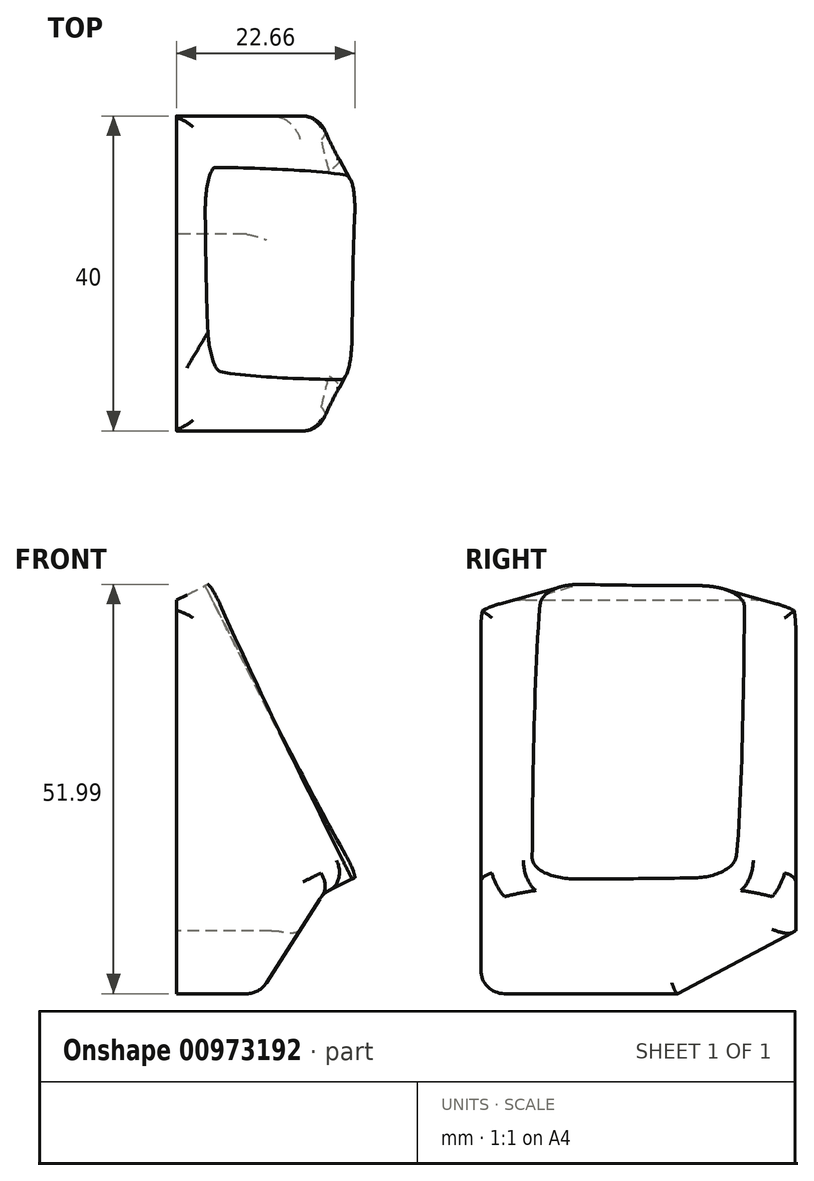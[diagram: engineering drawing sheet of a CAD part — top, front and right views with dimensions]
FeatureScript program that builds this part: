
annotation { "Feature Type Name" : "Feature", "Feature Type Description" : "" }
export const myFeature = defineFeature(function(context is Context, id is Id, definition is map)
    precondition{}
    {
        {
            var Q0;
            Q0=qCreatedBy(makeId("Front.planeOp"),FACE);
            var sketch = newSketch(context, id + "F0", { "sketchPlane" : qUnion([Q0])});
            skLineSegment(sketch, "E0", {"start": v(-46.03, 26.47) * mm, "end": v(-46.03, -23.53) * mm});
            skPoint(sketch, "E1", {"position": v(-35.49, -23.53) * mm});
            skPoint(sketch, "E2", {"position": v(-27.37, -10.8) * mm});
            skLineSegment(sketch, "E3", {"start": v(-27.37, -10.8) * mm, "end": v(-35.49, -23.53) * mm});
            skLineSegment(sketch, "E4", {"start": v(-46.03, -23.53) * mm, "end": v(-35.49, -23.53) * mm});
            skLineSegment(sketch, "E5", {"start": v(-46.03, 26.47) * mm, "end": v(-27.37, -10.8) * mm});
            skLineSegment(sketch, "E6", {"start": v(-46.03, 26.47) * mm, "end": v(-41.55, 28.7) * mm});
            skLineSegment(sketch, "E7", {"start": v(-27.37, -10.8) * mm, "end": v(-22.9, -8.55) * mm});
            skLineSegment(sketch, "E8", {"start": v(-41.55, 28.7) * mm, "end": v(-22.9, -8.55) * mm});
            skSolve(sketch);
        }
        {
            var Q0;
            Q0=makeQuery(id+"F0.imprint","IMPRINT",FACE,{"disambiguationData":[TD([[makeQuery(id+"F0.imprint","IMPRINT",EDGE,{"derivedFrom":sQuery(id+"F0.wireOp",EDGE,"E0")}),1.0]])]});
            extrude(context, id + "F1", {"entities" : qUnion([Q0]), "depth" : 40 * mm, "offsetDistance" : 25.4 * mm});
        }
        {
            var Q0;
            Q0=makeQuery(id+"F0.imprint","IMPRINT",FACE,{"disambiguationData":[TD([[makeQuery(id+"F0.imprint","IMPRINT",EDGE,{"derivedFrom":sQuery(id+"F0.wireOp",EDGE,"E5")}),1.0]])]});
            extrude(context, id + "F2", {"entities" : qUnion([Q0]), "operationType" : NewBodyOperationType.ADD, "depth" : 32 * mm, "offsetDistance" : 25 * mm});
        }
        {
            var Q0;
            Q0=makeQuery(id+"F0.imprint","IMPRINT",FACE,{"disambiguationData":[TD([[makeQuery(id+"F0.imprint","IMPRINT",EDGE,{"derivedFrom":sQuery(id+"F0.wireOp",EDGE,"E5")}),1.0]])]});
            extrude(context, id + "F3", {"entities" : qUnion([Q0]), "operationType" : NewBodyOperationType.REMOVE, "depth" : 8 * mm, "offsetDistance" : 25 * mm});
        }
        {
            var Q0;
            Q0=makeQuery(id+"F2.opExtrude","SWEPT_FACE",FACE,{"disambiguationData":[OSD([sQuery(id+"F0.wireOp",EDGE,"E7")])]});
            var sketch = newSketch(context, id + "F4", { "sketchPlane" : qUnion([Q0])});
            skPoint(sketch, "E9.0", {"position": v(-24.3, 32) * mm});
            skPoint(sketch, "E10.0", {"position": v(-29.3, 40) * mm});
            skPoint(sketch, "E11.0", {"position": v(-29.3, 32) * mm});
            skPoint(sketch, "E12.0", {"position": v(-24.3, 8) * mm});
            skPoint(sketch, "E13.0", {"position": v(-29.3, 8) * mm});
            skPoint(sketch, "E14.0", {"position": v(-29.3, 0) * mm});
            skLineSegment(sketch, "E15", {"start": v(-24.3, 32) * mm, "end": v(-29.3, 40) * mm});
            skLineSegment(sketch, "E16", {"start": v(-29.3, 32) * mm, "end": v(-24.3, 32) * mm});
            skLineSegment(sketch, "E17", {"start": v(-24.3, 8) * mm, "end": v(-29.3, 8) * mm});
            skLineSegment(sketch, "E18", {"start": v(-29.3, 0) * mm, "end": v(-24.3, 8) * mm});
            skLineSegment(sketch, "E19", {"start": v(-29.3, 40) * mm, "end": v(-29.3, 32) * mm});
            skLineSegment(sketch, "E20", {"start": v(-29.3, 8) * mm, "end": v(-29.3, 0) * mm});
            skSolve(sketch);
        }
        {
            var Q0;
            Q0=makeQuery(id+"F4.imprint","IMPRINT",FACE,{"disambiguationData":[TD([[makeQuery(id+"F4.imprint","IMPRINT",EDGE,{"derivedFrom":sQuery(id+"F4.wireOp",EDGE,"E15")}),1.0]])]});
            var Q1;
            Q1=makeQuery(id+"F4.imprint","IMPRINT",FACE,{"disambiguationData":[TD([[makeQuery(id+"F4.imprint","IMPRINT",EDGE,{"derivedFrom":sQuery(id+"F4.wireOp",EDGE,"E17")}),-1.0]])]});
            extrude(context, id + "F5", {"entities" : qUnion([Q0, Q1]), "operationType" : NewBodyOperationType.ADD, "oppositeDirection" : true, "depth" : 41.67 * mm, "offsetDistance" : 25 * mm});
        }
        {
            var Q0;
            Q0=makeQuery(id+"F2.opExtrude","SWEPT_FACE",FACE,{"disambiguationData":[OSD([sQuery(id+"F0.wireOp",EDGE,"E8")])]});
            cPlane(context, id + "F6", {"entities" : qUnion([Q0]), "cplaneType" : CPlaneType.OFFSET, "offset" : 0 * mm, "width" : 150 * mm, "height" : 150 * mm});
        }
        {
            var Q0;
            Q0=qCreatedBy(id+"F6.planeOp",FACE);
            var sketch = newSketch(context, id + "F7", { "sketchPlane" : qUnion([Q0])});
            skPoint(sketch, "E21.0", {"position": v(-32, 2.6) * mm});
            skPoint(sketch, "E22.0", {"position": v(-8, 44.28) * mm});
            skLineSegment(sketch, "E23", {"start": v(-32, 2.6) * mm, "end": v(-8, 44.28) * mm});
            skSolve(sketch);
        }
        {
            var Q0;
            Q0=sQuery(id+"F7.wireOp",VERTEX,"E21.0");
            var Q1;
            Q1=sQuery(id+"F7.wireOp",EDGE,"E23");
            cPlane(context, id + "F8", {"entities" : qUnion([Q0, Q1]), "cplaneType" : CPlaneType.LINE_POINT, "offset" : 25 * mm, "width" : 150 * mm, "height" : 150 * mm});
        }
        {
            var Q0;
            Q0=qCreatedBy(id+"F8.planeOp",FACE);
            var sketch = newSketch(context, id + "F9", { "sketchPlane" : qUnion([Q0])});
            skPoint(sketch, "E24.0", {"position": v(-35.66, -42.45) * mm});
            skPoint(sketch, "E25.0", {"position": v(-25.57, -2.1) * mm});
            skPoint(sketch, "E26.0", {"position": v(-30.62, -22.27) * mm});
            skEllipse(sketch, "E27", {"center": v(-30.62, -22.27) * mm, "majorRadius": 20.8 * mm, "minorRadius": 0.93 * mm, "majorAxis": v(0.24, 0.97)});
            skSolve(sketch);
        }
        {
            var Q0;
            Q0=makeQuery(id+"F9.imprint","IMPRINT",FACE,{"disambiguationData":[TD([[makeQuery(id+"F9.imprint","IMPRINT",EDGE,{"derivedFrom":sQuery(id+"F9.wireOp",EDGE,"E27")}),1.0]])]});
            extrude(context, id + "F10", {"entities" : qUnion([Q0]), "operationType" : NewBodyOperationType.REMOVE, "depth" : 70 * mm, "offsetDistance" : 25 * mm, "hasSecondDirection" : true, "secondDirectionOppositeDirection" : true, "secondDirectionDepth" : 10 * mm});
        }
        {
            var Q0;
            Q0=makeQuery(id+"F1.opExtrude","SWEPT_FACE",FACE,{"disambiguationData":[OSD([sQuery(id+"F0.wireOp",EDGE,"E0")])]});
            var sketch = newSketch(context, id + "F11", { "sketchPlane" : qUnion([Q0])});
            skPoint(sketch, "E28.0", {"position": v(20, -23.53) * mm});
            skPoint(sketch, "E29.0", {"position": v(0, 1.47) * mm});
            skPoint(sketch, "E30", {"position": v(0, -15.53) * mm});
            skPoint(sketch, "E31", {"position": v(15, -23.53) * mm});
            skPoint(sketch, "E32", {"position": v(0, -23.53) * mm});
            skLineSegment(sketch, "E33", {"start": v(0, -15.53) * mm, "end": v(15, -23.53) * mm});
            skLineSegment(sketch, "E34", {"start": v(0, -23.53) * mm, "end": v(0, -15.53) * mm});
            skLineSegment(sketch, "E35", {"start": v(15, -23.53) * mm, "end": v(0, -23.53) * mm});
            skSolve(sketch);
        }
        {
            var Q0;
            {var subQ0=sQuery(id+"F11.wireOp",EDGE,"E33");Q0=makeQuery(id+"F11.imprint","IMPRINT",FACE,{"disambiguationData":[TD([[makeQuery(id+"F11.imprint","IMPRINT",EDGE,{"derivedFrom":subQ0}),-1.0]])]});}
            extrude(context, id + "F12", {"entities" : qUnion([Q0]), "operationType" : NewBodyOperationType.REMOVE, "oppositeDirection" : true, "depth" : 25 * mm, "offsetDistance" : 25 * mm});
        }
        {
            var Q0;
            Q0=makeQuery(id+"F5.opExtrude","CAP_EDGE",EDGE,{"disambiguationData":[OSD([sQuery(id+"F4.wireOp",EDGE,"E15")])],"isStart":true});
            var Q1;
            Q1=makeQuery(id+"F5.opExtrude","CAP_EDGE",EDGE,{"disambiguationData":[OSD([sQuery(id+"F4.wireOp",EDGE,"E18")])],"isStart":true});
            var Q2;
            Q2=makeQuery(id+"F1.opExtrude","CAP_EDGE",EDGE,{"disambiguationData":[OSD([sQuery(id+"F0.wireOp",EDGE,"E3")])],"isStart":true});
            var Q3;
            Q3=makeQuery(id+"F5.boolean.opBoolean","MERGE",EDGE,{"derivedFrom":[makeQuery(id+"F3.boolean.opBoolean","COPY",EDGE,{"derivedFrom":makeQuery(id+"F3.opExtrude","CAP_EDGE",EDGE,{"disambiguationData":[OSD([sQuery(id+"F0.wireOp",EDGE,"E5")])],"isStart":true})}),makeQuery(id+"F5.opExtrude","SWEPT_EDGE",EDGE,{"disambiguationData":[OSD([sQuery(id+"F4.wireOp",EDGE,"E18"),sQuery(id+"F4.wireOp",EDGE,"E20")])]})]});
            var Q4;
            {var subQ0=sQuery(id+"F0.wireOp",EDGE,"E7");var subQ1=sQuery(id+"F0.wireOp",EDGE,"E5");var subQ2=sQuery(id+"F0.wireOp",EDGE,"E3");var subQ3=makeQuery(id+"F1.opExtrude","SWEPT_EDGE",EDGE,{"disambiguationData":[OSD([subQ2,subQ1,subQ0])]});var subQ4=makeQuery(id+"F2.boolean.opBoolean","MERGE",EDGE,{"derivedFrom":[subQ3,makeQuery(id+"F2.opExtrude","SWEPT_EDGE",EDGE,{"disambiguationData":[OSD([subQ2,subQ1,subQ0])]})]});Q4=makeQuery(id+"F5.boolean.opBoolean","MERGE",EDGE,{"derivedFrom":[makeQuery(id+"F2.boolean.opBoolean","SPLIT",EDGE,{"derivedFrom":subQ3}),makeQuery(id+"F3.boolean.opBoolean","MERGE",EDGE,{"derivedFrom":[subQ4],"fromTools":[makeQuery(id+"F3.opExtrude","SWEPT_EDGE",EDGE,{"disambiguationData":[OSD([subQ2,subQ1,subQ0])]})]}),makeQuery(id+"F3.boolean.opBoolean","SPLIT",EDGE,{"derivedFrom":subQ4}),makeQuery(id+"F5.opExtrude","CAP_EDGE",EDGE,{"disambiguationData":[OSD([sQuery(id+"F4.wireOp",EDGE,"E19")])],"isStart":true}),makeQuery(id+"F5.opExtrude","CAP_EDGE",EDGE,{"disambiguationData":[OSD([sQuery(id+"F4.wireOp",EDGE,"E20")])],"isStart":true})]});}
            var Q5;
            Q5=makeQuery(id+"F1.opExtrude","CAP_EDGE",EDGE,{"disambiguationData":[OSD([sQuery(id+"F0.wireOp",EDGE,"E3")])],"isStart":false});
            var Q6;
            Q6=makeQuery(id+"F5.boolean.opBoolean","MERGE",EDGE,{"derivedFrom":[makeQuery(id+"F1.opExtrude","CAP_EDGE",EDGE,{"disambiguationData":[OSD([sQuery(id+"F0.wireOp",EDGE,"E5")])],"isStart":false}),makeQuery(id+"F5.opExtrude","SWEPT_EDGE",EDGE,{"disambiguationData":[OSD([sQuery(id+"F4.wireOp",EDGE,"E15"),sQuery(id+"F4.wireOp",EDGE,"E19")])]})]});
            var Q7;
            Q7=makeQuery(id+"F1.opExtrude","SWEPT_EDGE",EDGE,{"disambiguationData":[OSD([sQuery(id+"F0.wireOp",EDGE,"E3"),sQuery(id+"F0.wireOp",EDGE,"E4")])]});
            var Q8;
            Q8=makeQuery(id+"F5.opExtrude","CAP_EDGE",EDGE,{"disambiguationData":[OSD([sQuery(id+"F4.wireOp",EDGE,"E18")])],"isStart":false});
            var Q9;
            Q9=makeQuery(id+"F5.opExtrude","CAP_EDGE",EDGE,{"disambiguationData":[OSD([sQuery(id+"F4.wireOp",EDGE,"E15")])],"isStart":false});
            var Q10;
            Q10=makeQuery(id+"F1.opExtrude","CAP_EDGE",EDGE,{"disambiguationData":[OSD([sQuery(id+"F0.wireOp",EDGE,"E4")])],"isStart":false});
            var Q11;
            Q11=makeQuery(id+"F1.opExtrude","CAP_EDGE",EDGE,{"disambiguationData":[OSD([sQuery(id+"F0.wireOp",EDGE,"E4")])],"isStart":true});
            var Q12;
            Q12=makeQuery(id+"F12.boolean.opBoolean","COPY",EDGE,{"derivedFrom":makeQuery(id+"F12.opExtrude","SWEPT_EDGE",EDGE,{"disambiguationData":[OSD([sQuery(id+"F0.wireOp",EDGE,"E0"),sQuery(id+"F11.wireOp",EDGE,"E33"),sQuery(id+"F11.wireOp",EDGE,"E34")])]})});
            var Q13;
            Q13=makeQuery(id+"F12.boolean.opBoolean","INTERSECT",EDGE,{"derivedFrom":[makeQuery(id+"F1.opExtrude","SWEPT_FACE",FACE,{"disambiguationData":[OSD([sQuery(id+"F0.wireOp",EDGE,"E3")])]}),makeQuery(id+"F12.opExtrude","SWEPT_FACE",FACE,{"disambiguationData":[OSD([sQuery(id+"F11.wireOp",EDGE,"E33")])]})]});
            var Q14;
            Q14=makeQuery(id+"F12.boolean.opBoolean","COPY",EDGE,{"derivedFrom":makeQuery(id+"F12.opExtrude","SWEPT_EDGE",EDGE,{"disambiguationData":[OSD([sQuery(id+"F0.wireOp",EDGE,"E0"),sQuery(id+"F0.wireOp",EDGE,"E4"),sQuery(id+"F11.wireOp",EDGE,"E33"),sQuery(id+"F11.wireOp",EDGE,"E35")])]})});
            fillet(context, id + "F13", {"entities" : qUnion([Q0, Q1, Q2, Q3, Q4, Q5, Q6, Q7, Q8, Q9, Q10, Q11, Q12, Q13, Q14]), "radius" : 3 * mm, "tangentPropagation" : true, "allowEdgeOverflow" : false});
        }
    });
